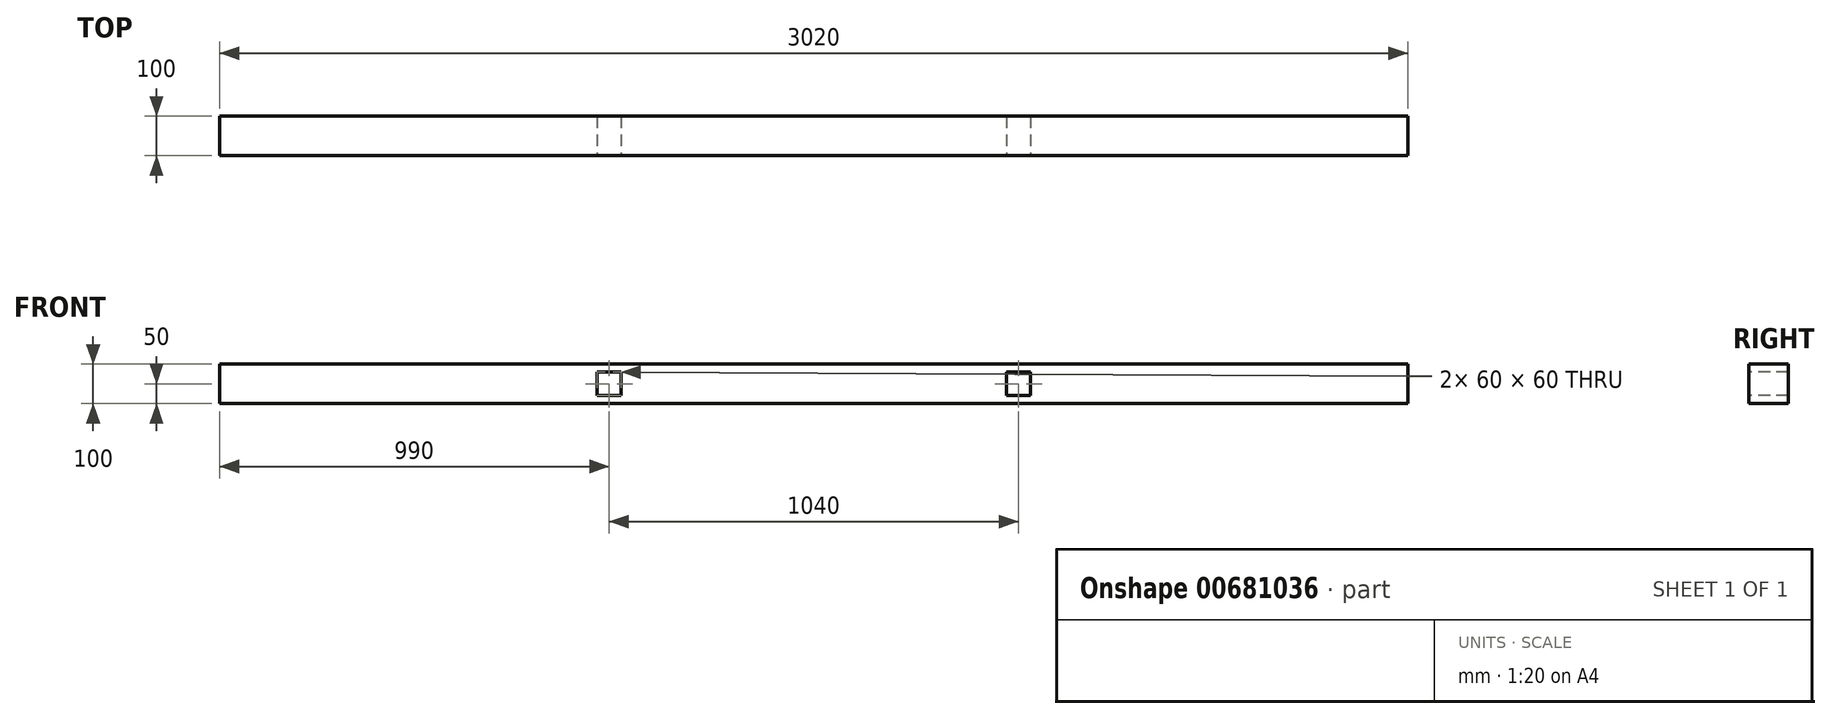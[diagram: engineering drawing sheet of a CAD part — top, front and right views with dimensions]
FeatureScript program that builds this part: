
annotation { "Feature Type Name" : "Feature", "Feature Type Description" : "" }
export const myFeature = defineFeature(function(context is Context, id is Id, definition is map)
    precondition{}
    {
        {
            var Q0;
            Q0=qCreatedBy(makeId("Front.planeOp"),FACE);
            var sketch = newSketch(context, id + "F0", { "sketchPlane" : qUnion([Q0])});
            skLineSegment(sketch, "E0.bottom", {"start": v(0, 0) * mm, "end": v(3020, 0) * mm});
            skLineSegment(sketch, "E0.top", {"start": v(0, 100) * mm, "end": v(3020, 100) * mm});
            skLineSegment(sketch, "E0.left", {"start": v(0, 0) * mm, "end": v(0, 100) * mm});
            skLineSegment(sketch, "E0.right", {"start": v(3020, 0) * mm, "end": v(3020, 100) * mm});
            skSolve(sketch);
        }
        {
            var Q0;
            Q0=qSketchRegion(id+"F0",true);
            extrude(context, id + "F1", {"entities" : qUnion([Q0]), "depth" : 100 * mm, "offsetDistance" : 25 * mm});
        }
        {
            var Q0;
            Q0=makeQuery(id+"F1.opExtrude","CAP_FACE",FACE,{"disambiguationData":[OSD([sQuery(id+"F0.wireOp",EDGE,"E0.bottom"),sQuery(id+"F0.wireOp",EDGE,"E0.top"),sQuery(id+"F0.wireOp",EDGE,"E0.left"),sQuery(id+"F0.wireOp",EDGE,"E0.right")])],"isStart":false});
            var sketch = newSketch(context, id + "F2", { "sketchPlane" : qUnion([Q0])});
            skLineSegment(sketch, "E1.bottom", {"start": v(960, 80) * mm, "end": v(1020, 80) * mm});
            skLineSegment(sketch, "E1.top", {"start": v(960, 20) * mm, "end": v(1020, 20) * mm});
            skLineSegment(sketch, "E1.left", {"start": v(960, 80) * mm, "end": v(960, 20) * mm});
            skLineSegment(sketch, "E1.right", {"start": v(1020, 80) * mm, "end": v(1020, 20) * mm});
            skLineSegment(sketch, "E2.bottom", {"start": v(2000, 80) * mm, "end": v(2060, 80) * mm});
            skLineSegment(sketch, "E2.top", {"start": v(2000, 20) * mm, "end": v(2060, 20) * mm});
            skLineSegment(sketch, "E2.left", {"start": v(2000, 80) * mm, "end": v(2000, 20) * mm});
            skLineSegment(sketch, "E2.right", {"start": v(2060, 80) * mm, "end": v(2060, 20) * mm});
            skSolve(sketch);
        }
        {
            var Q0;
            Q0=qSketchRegion(id+"F2",true);
            extrude(context, id + "F3", {"entities" : qUnion([Q0]), "operationType" : NewBodyOperationType.REMOVE, "endBound" : BoundingType.THROUGH_ALL, "oppositeDirection" : true, "depth" : 25 * mm, "offsetDistance" : 25 * mm});
        }
    });
